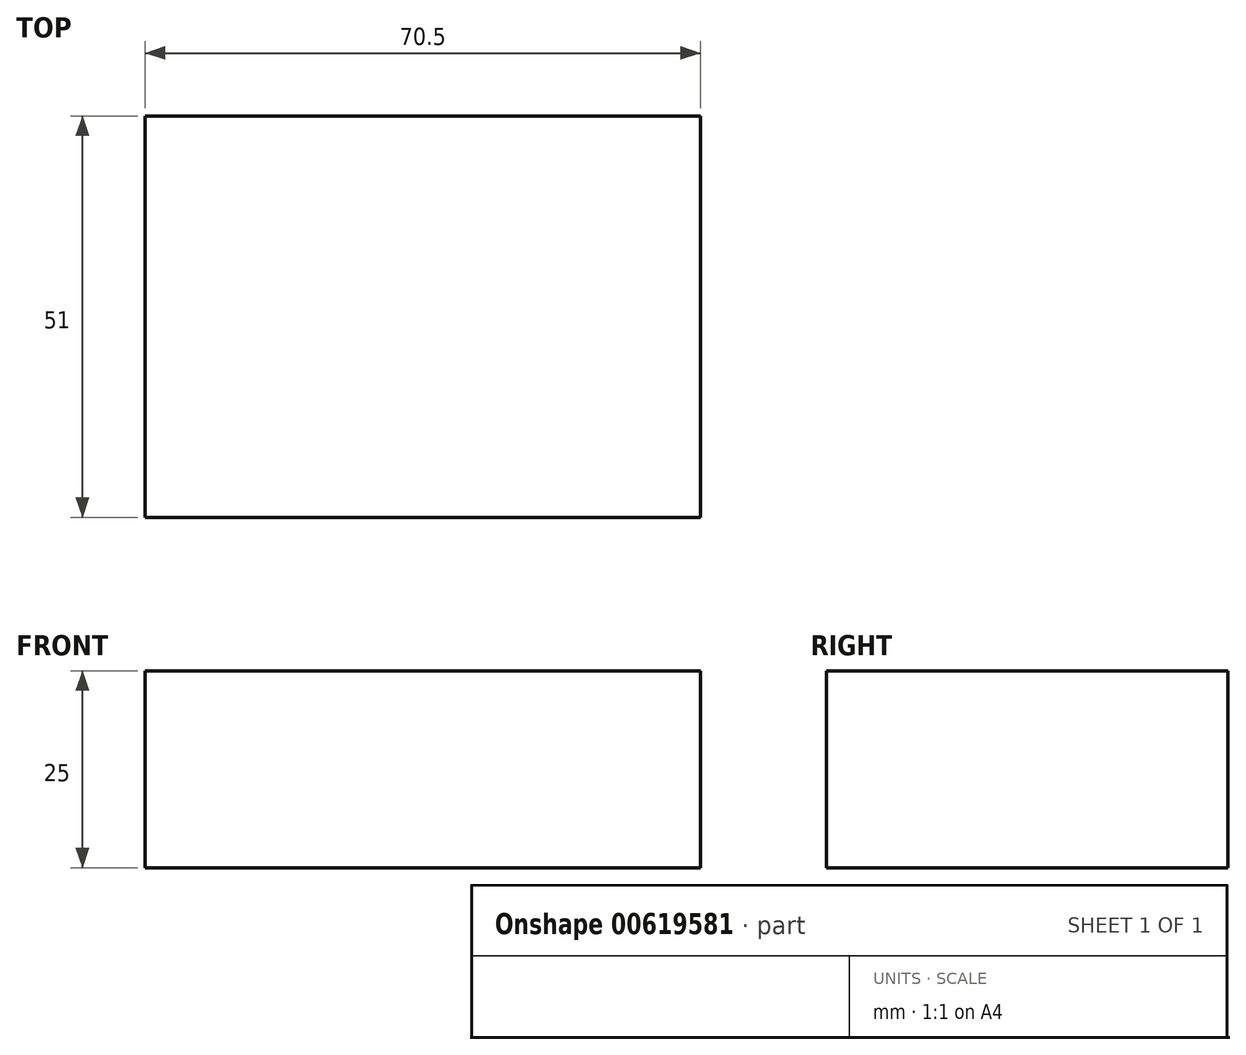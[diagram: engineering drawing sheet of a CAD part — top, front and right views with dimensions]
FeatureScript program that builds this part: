
annotation { "Feature Type Name" : "Feature", "Feature Type Description" : "" }
export const myFeature = defineFeature(function(context is Context, id is Id, definition is map)
    precondition{}
    {
        {
            var Q0;
            Q0=qCreatedBy(makeId("Top.planeOp"),FACE);
            var sketch = newSketch(context, id + "F0", { "sketchPlane" : qUnion([Q0])});
            skLineSegment(sketch, "E0.bottom", {"start": v(35.25, 25.5) * mm, "end": v(-35.25, 25.5) * mm});
            skLineSegment(sketch, "E0.top", {"start": v(35.25, -25.5) * mm, "end": v(-35.25, -25.5) * mm});
            skLineSegment(sketch, "E0.left", {"start": v(35.25, 25.5) * mm, "end": v(35.25, -25.5) * mm});
            skLineSegment(sketch, "E0.right", {"start": v(-35.25, 25.5) * mm, "end": v(-35.25, -25.5) * mm});
            skPoint(sketch, "E0.middle", {"position": v(0, 0) * mm});
            skSolve(sketch);
        }
        {
            var Q0;
            Q0=makeQuery(id+"F0.imprint","IMPRINT",FACE,{"disambiguationData":[TD([[makeQuery(id+"F0.imprint","IMPRINT",EDGE,{"derivedFrom":sQuery(id+"F0.wireOp",EDGE,"E0.bottom")}),1.0]])]});
            extrude(context, id + "F1", {"entities" : qUnion([Q0]), "depth" : 25 * mm, "offsetDistance" : 25 * mm});
        }
    });
